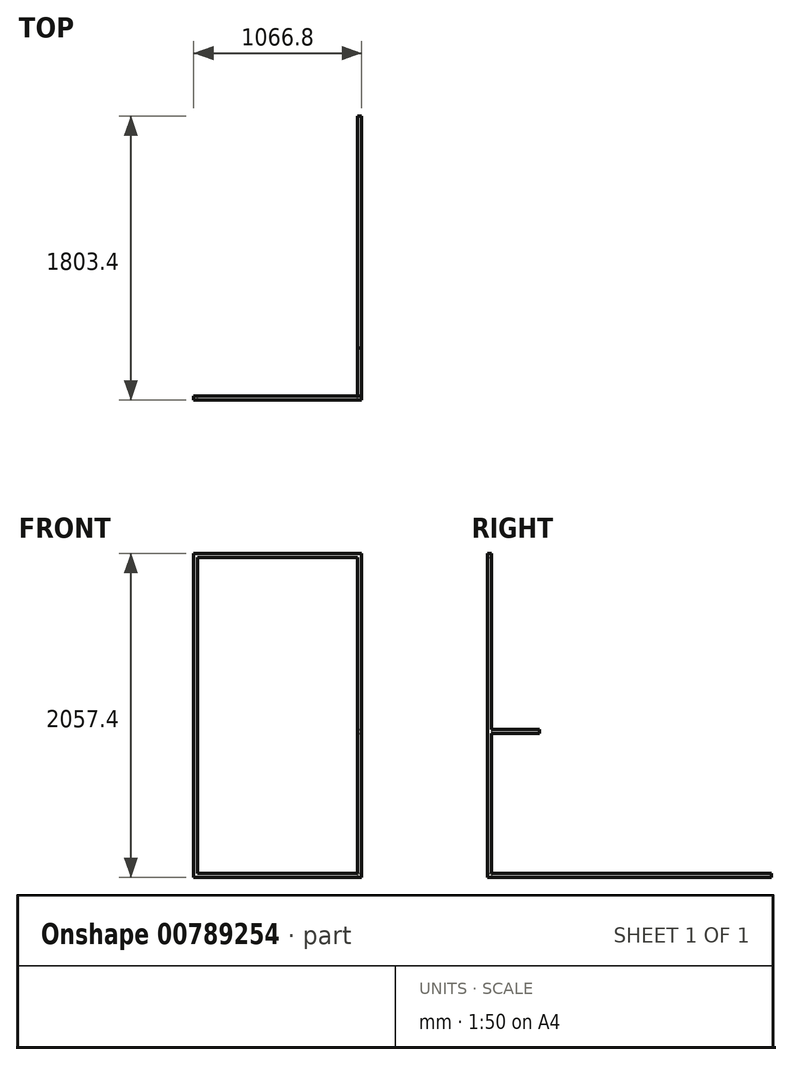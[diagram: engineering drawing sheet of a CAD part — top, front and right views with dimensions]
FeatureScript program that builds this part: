
annotation { "Feature Type Name" : "Feature", "Feature Type Description" : "" }
export const myFeature = defineFeature(function(context is Context, id is Id, definition is map)
    precondition{}
    {
        {
            var Q0;
            Q0=qCreatedBy(makeId("Front.planeOp"),FACE);
            var sketch = newSketch(context, id + "F0", { "sketchPlane" : qUnion([Q0])});
            skLineSegment(sketch, "E0.bottom", {"start": v(533.4, 1028.7) * mm, "end": v(-533.4, 1028.7) * mm});
            skLineSegment(sketch, "E0.top", {"start": v(533.4, -1028.7) * mm, "end": v(-533.4, -1028.7) * mm});
            skLineSegment(sketch, "E0.left", {"start": v(533.4, 1028.7) * mm, "end": v(533.4, -1028.7) * mm});
            skLineSegment(sketch, "E0.right", {"start": v(-533.4, 1028.7) * mm, "end": v(-533.4, -1028.7) * mm});
            skPoint(sketch, "E0.middle", {"position": v(0, 0) * mm});
            skLineSegment(sketch, "E1.bottom", {"start": v(508, 1003.3) * mm, "end": v(-508, 1003.3) * mm});
            skLineSegment(sketch, "E1.top", {"start": v(508, -1003.3) * mm, "end": v(-508, -1003.3) * mm});
            skLineSegment(sketch, "E1.left", {"start": v(508, 1003.3) * mm, "end": v(508, -1003.3) * mm});
            skLineSegment(sketch, "E1.right", {"start": v(-508, 1003.3) * mm, "end": v(-508, -1003.3) * mm});
            skSolve(sketch);
        }
        {
            var Q0;
            Q0 = qSketchRegion(id + "F0", true);
            extrude(context, id + "F1", {"entities" : qUnion([Q0]), "depth" : 25.4 * mm, "offsetDistance" : 25.4 * mm});
        }
        {
            var Q0;
            Q0=makeQuery(id+"F1.opExtrude","SWEPT_FACE",FACE,{"disambiguationData":[OSD([sQuery(id+"F0.wireOp",EDGE,"E0.left")])]});
            var sketch = newSketch(context, id + "F2", { "sketchPlane" : qUnion([Q0])});
            skLineSegment(sketch, "E2.bottom", {"start": v(0, -114.3) * mm, "end": v(304.8, -114.3) * mm});
            skLineSegment(sketch, "E2.top", {"start": v(0, -88.9) * mm, "end": v(304.8, -88.9) * mm});
            skLineSegment(sketch, "E2.left", {"start": v(0, -114.3) * mm, "end": v(0, -88.9) * mm});
            skLineSegment(sketch, "E2.right", {"start": v(304.8, -114.3) * mm, "end": v(304.8, -88.9) * mm});
            skSolve(sketch);
        }
        {
            var Q0;
            Q0 = qSketchRegion(id + "F2", true);
            extrude(context, id + "F3", {"entities" : qUnion([Q0]), "operationType" : NewBodyOperationType.ADD, "oppositeDirection" : true, "depth" : 25.4 * mm, "offsetDistance" : 25.4 * mm});
        }
        {
            var Q0;
            Q0=makeQuery(id+"F1.opExtrude","CAP_FACE",FACE,{"disambiguationData":[OSD([sQuery(id+"F0.wireOp",EDGE,"E0.bottom"),sQuery(id+"F0.wireOp",EDGE,"E0.top"),sQuery(id+"F0.wireOp",EDGE,"E0.left"),sQuery(id+"F0.wireOp",EDGE,"E0.right"),sQuery(id+"F0.wireOp",EDGE,"E1.bottom"),sQuery(id+"F0.wireOp",EDGE,"E1.top"),sQuery(id+"F0.wireOp",EDGE,"E1.left"),sQuery(id+"F0.wireOp",EDGE,"E1.right")])],"isStart":true});
            var sketch = newSketch(context, id + "F4", { "sketchPlane" : qUnion([Q0])});
            skLineSegment(sketch, "E3.bottom", {"start": v(-508, -1003.3) * mm, "end": v(-533.4, -1003.3) * mm});
            skLineSegment(sketch, "E3.top", {"start": v(-508, -1028.7) * mm, "end": v(-533.4, -1028.7) * mm});
            skLineSegment(sketch, "E3.left", {"start": v(-508, -1003.3) * mm, "end": v(-508, -1028.7) * mm});
            skLineSegment(sketch, "E3.right", {"start": v(-533.4, -1003.3) * mm, "end": v(-533.4, -1028.7) * mm});
            skSolve(sketch);
        }
        {
            var Q0;
            Q0 = qSketchRegion(id + "F4", true);
            extrude(context, id + "F5", {"entities" : qUnion([Q0]), "operationType" : NewBodyOperationType.ADD, "depth" : 1778 * mm, "offsetDistance" : 25.4 * mm});
        }
    });
